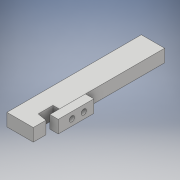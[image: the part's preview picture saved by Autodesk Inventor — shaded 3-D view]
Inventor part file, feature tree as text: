
AUTODESK INVENTOR PART (.ipt)
format: ipt  version: 2018 (Build 220112000, 112)  size: 129,024 bytes
history: native  units: mm
features: sketch x3, extrude x2, hole x1
ambient origin geometry x8: Origin, YZ Plane, XZ Plane, XY Plane, X Axis, Y Axis, Z Axis, Center Point
bodies: Solid1 (feature_tree), Solid2 (feature_tree)
feature tree (6):
  extrude  "Extrusion1"  Depth=6.0mm
  extrude  "Extrusion2"  Depth=12.0mm
  hole  "Hole1"  [1 undecoded]
  sketch  "Sketch1"  dims[d1=14.0mm d2=6.0mm]
  sketch  "Sketch2"  dims[d3=12.0mm d4=17.453293mm]
  sketch  "Sketch3"  dims[d5=9.0mm d6=25.0mm d7=12.0mm d8=0.0mm d9=100.0mm d11=9.0mm d12=5.0mm d13=5.0mm d14=8.0mm d15=0.0mm d16=5.0mm d17=6.0mm d18=4.0mm d19=2.0mm d20=90.0deg d21=8.0mm d22=20.594885mm]
note: 1 required parameter value undecoded (feature->parameter linkage not recoverable at this tier; creation-order binding heuristic only, values carry confidence <= 0.55)
